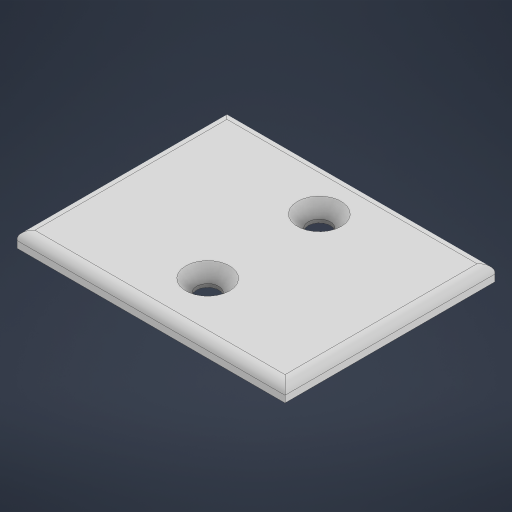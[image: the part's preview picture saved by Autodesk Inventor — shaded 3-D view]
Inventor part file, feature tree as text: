
AUTODESK INVENTOR PART (.ipt)
format: ipt  version: 2024 (Build 280153000, 153)  size: 193,536 bytes
history: native  units: in
note: dims shown in document units (in); Inventor stores cm internally (conversion verified against a paired STEP export)
features: sketch x2, extrude x1, hole x1, fillet x1
ambient origin geometry x8: Origin, YZ Plane, XZ Plane, XY Plane, X Axis, Y Axis, Z Axis, Center Point
bodies: Solid1 (feature_tree)
feature tree (5):
  extrude  "Extrusion1"  Depth=1.8504in
  hole  "Hole1"  [1 undecoded]
  fillet  "Fillet2"  Radius=0.4724in
  sketch  "Sketch1"  dims[d0=2.3622in d1=1.8504in]
  sketch  "Sketch2"  dims[d7=0.1378in d8=0.0in d10=0.9843in d11=0.4724in d12=0.3937in d13=0.196in d14=0.2362in d15=0.385in d16=0.0787in d17=0.5635in d18=0.315in d19=0.8108in d20=0.0787in]
note: 1 required parameter value undecoded (feature->parameter linkage not recoverable at this tier; creation-order binding heuristic only, values carry confidence <= 0.55)
